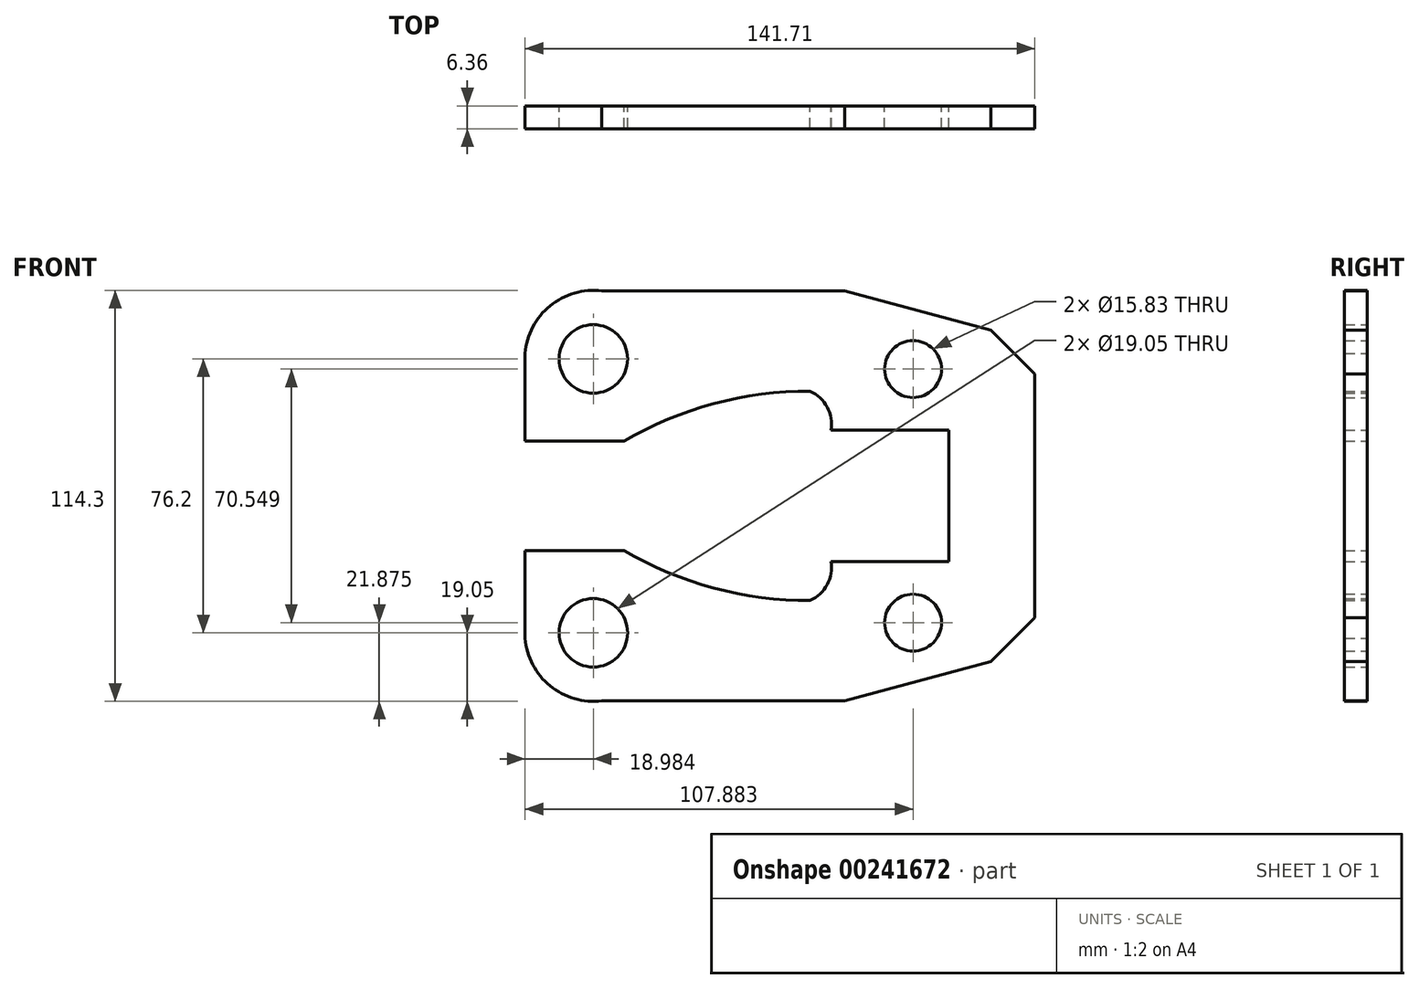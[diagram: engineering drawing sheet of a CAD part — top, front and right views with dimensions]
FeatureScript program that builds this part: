
annotation { "Feature Type Name" : "Feature", "Feature Type Description" : "" }
export const myFeature = defineFeature(function(context is Context, id is Id, definition is map)
    precondition{}
    {
        {
            var Q0;
            Q0=qCreatedBy(makeId("Front.planeOp"),FACE);
            var sketch = newSketch(context, id + "F0", { "sketchPlane" : qUnion([Q0])});
            skLineSegment(sketch, "E0", {"start": v(-62.68, 57) * mm, "end": v(9.6, 57) * mm});
            skLineSegment(sketch, "E1", {"start": v(9.6, 57) * mm, "end": v(50.25, 46.11) * mm});
            skLineSegment(sketch, "E2", {"start": v(50.25, 46.11) * mm, "end": v(62.42, 33.94) * mm});
            skLineSegment(sketch, "E3", {"start": v(62.42, 33.94) * mm, "end": v(62.42, -5.23) * mm});
            skLineSegment(sketch, "E4", {"start": v(-79.3, 39.65) * mm, "end": v(-79.3, 15.24) * mm});
            skArc(sketch, "E5", {"start": v(0, 29.11) * mm, "mid": v(-26.8, 25.65) * mm, "end": v(-51.75, 15.24) * mm});
            skArc(sketch, "E6", {"start": v(5.8, 18.28) * mm, "mid": v(4.73, 24.67) * mm, "end": v(0, 29.11) * mm});
            skPoint(sketch, "E6.startSnap0", {"position": v(-46.15, 18.28) * mm});
            skLineSegment(sketch, "E7", {"start": v(5.8, 18.28) * mm, "end": v(38.54, 18.28) * mm});
            skLineSegment(sketch, "E8", {"start": v(38.54, 18.28) * mm, "end": v(38.54, 0) * mm});
            skArc(sketch, "E9", {"start": v(-57.93, 57) * mm, "mid": v(-72.32, 52.89) * mm, "end": v(-79.3, 39.65) * mm});
            skCircle(sketch, "E10", {"center": v(-60.3, 38.1) * mm, "radius": 9.53 * mm});
            skCircle(sketch, "E11", {"center": v(28.6, 35.27) * mm, "radius": 7.91 * mm});
            skPoint(sketch, "E12.MirrorP", {"position": v(62.02, 9.74) * mm});
            skLineSegment(sketch, "E13", {"start": v(-51.75, 15.24) * mm, "end": v(-79.3, 15.24) * mm});
            skPoint(sketch, "E14.orphan", {"position": v(-79.3, 0) * mm});
            skPoint(sketch, "E15.orphan", {"position": v(-58.21, 0) * mm});
            skArc(sketch, "E16.MirrorCS", {"start": v(0, -29.11) * mm, "mid": v(-26.8, -25.65) * mm, "end": v(-51.75, -15.24) * mm});
            skCircle(sketch, "E17.MirrorC", {"center": v(-60.3, -38.1) * mm, "radius": 9.53 * mm});
            skLineSegment(sketch, "E18.MirrorCS", {"start": v(62.42, -33.94) * mm, "end": v(62.42, 5.23) * mm});
            skLineSegment(sketch, "E19.MirrorCS", {"start": v(-79.3, -39.65) * mm, "end": v(-79.3, -15.24) * mm});
            skLineSegment(sketch, "E20.MirrorCS", {"start": v(38.54, -18.28) * mm, "end": v(38.54, 0) * mm});
            skArc(sketch, "E21.MirrorCS", {"start": v(-57.93, -57) * mm, "mid": v(-72.32, -52.89) * mm, "end": v(-79.3, -39.65) * mm});
            skPoint(sketch, "E22.MirrorP", {"position": v(-46.15, -18.28) * mm});
            skPoint(sketch, "E23.MirrorP", {"position": v(62.02, -9.74) * mm});
            skLineSegment(sketch, "E24.MirrorCS", {"start": v(-62.68, -57) * mm, "end": v(9.6, -57) * mm});
            skLineSegment(sketch, "E25.MirrorCS", {"start": v(-51.75, -15.24) * mm, "end": v(-79.3, -15.24) * mm});
            skArc(sketch, "E26.MirrorCS", {"start": v(5.8, -18.28) * mm, "mid": v(4.73, -24.67) * mm, "end": v(0, -29.11) * mm});
            skLineSegment(sketch, "E27.MirrorCS", {"start": v(5.8, -18.28) * mm, "end": v(38.54, -18.28) * mm});
            skCircle(sketch, "E28.MirrorC", {"center": v(28.6, -35.27) * mm, "radius": 7.91 * mm});
            skLineSegment(sketch, "E29.MirrorCS", {"start": v(9.6, -57) * mm, "end": v(50.25, -46.11) * mm});
            skLineSegment(sketch, "E30.MirrorCS", {"start": v(50.25, -46.11) * mm, "end": v(62.42, -33.94) * mm});
            skSolve(sketch);
        }
        {
            var Q0;
            Q0 = qSketchRegion(id + "F0", true);
            extrude(context, id + "F1", {"entities" : qUnion([Q0]), "endBound" : BoundingType.SYMMETRIC, "depth" : 6.35 * mm});
        }
    });
